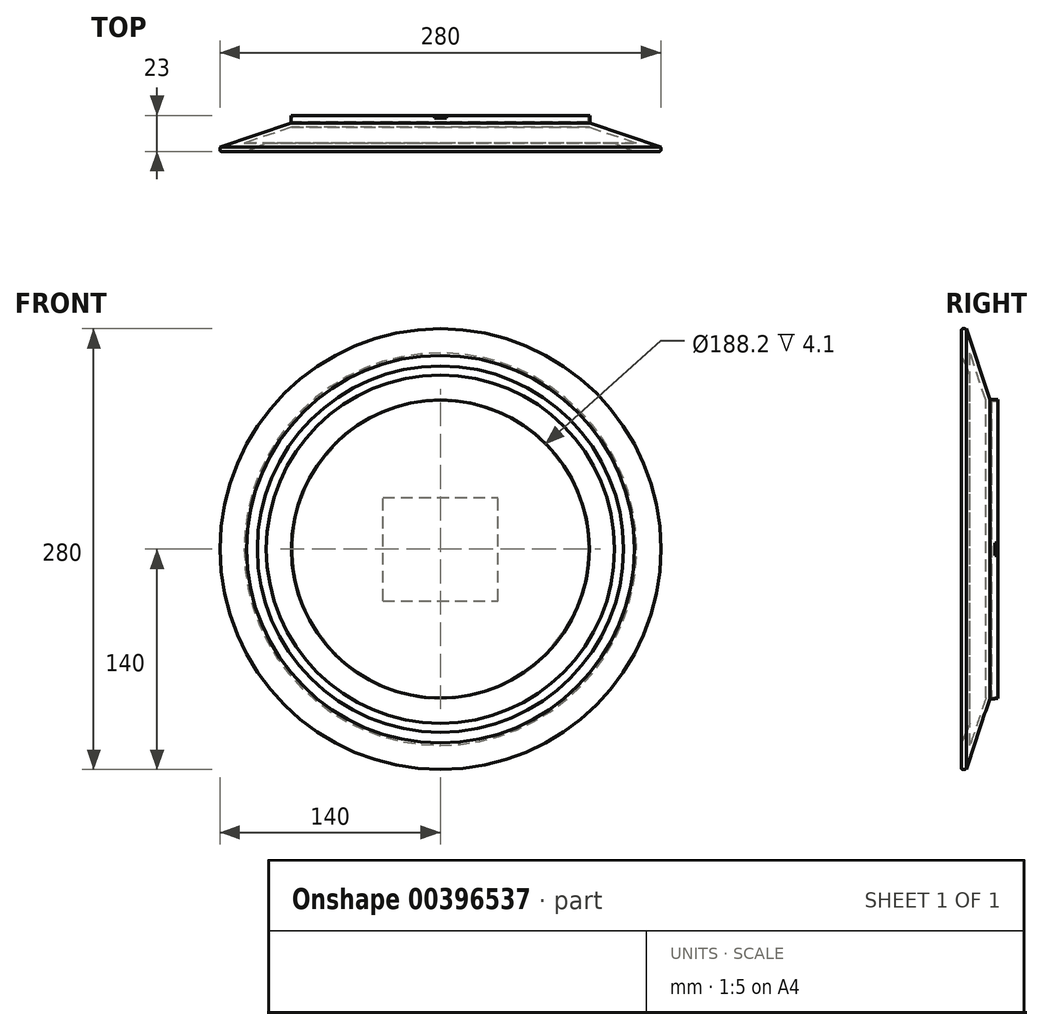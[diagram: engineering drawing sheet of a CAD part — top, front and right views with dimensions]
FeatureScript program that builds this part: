
annotation { "Feature Type Name" : "Feature", "Feature Type Description" : "" }
export const myFeature = defineFeature(function(context is Context, id is Id, definition is map)
    precondition{}
    {
        {
            var Q0;
            Q0=qCreatedBy(makeId("Front.planeOp"),FACE);
            var sketch = newSketch(context, id + "F0", { "sketchPlane" : qUnion([Q0])});
            skCircle(sketch, "E0", {"center": v(0, 0) * mm, "radius": 95 * mm});
            skSolve(sketch);
        }
        {
            var Q0;
            Q0=qSketchRegion(id+"F0",true);
            extrude(context, id + "F1", {"entities" : qUnion([Q0]), "depth" : 5 * mm});
        }
        {
            var Q0;
            Q0=makeQuery(id+"F1.opExtrude","CAP_FACE",FACE,{"disambiguationData":[OSD([sQuery(id+"F0.wireOp",EDGE,"E0")])],"isStart":true});
            shell(context, id + "F2", {"entities" : qUnion([Q0]), "thickness" : 0.9 * mm});
        }
        {
            var Q0;
            Q0=qCreatedBy(makeId("Front.planeOp"),FACE);
            cPlane(context, id + "F3", {"entities" : qUnion([Q0]), "cplaneType" : CPlaneType.OFFSET, "offset" : 20 * mm, "width" : 150 * mm, "height" : 150 * mm});
        }
        {
            var Q0;
            Q0=qCreatedBy(id+"F3.planeOp",FACE);
            var sketch = newSketch(context, id + "F4", { "sketchPlane" : qUnion([Q0])});
            skCircle(sketch, "E1", {"center": v(0, 0) * mm, "radius": 140 * mm});
            skSolve(sketch);
        }
        {
            var Q0;
            Q0=makeQuery(id+"F4.imprint","IMPRINT",FACE,{"disambiguationData":[TD([[makeQuery(id+"F4.imprint","IMPRINT",EDGE,{"derivedFrom":sQuery(id+"F4.wireOp",EDGE,"E1")}),1.0]])]});
            extrude(context, id + "F5", {"entities" : qUnion([Q0]), "depth" : 3 * mm});
        }
        {
            var Q0;
            Q0=makeQuery(id+"F1.opExtrude","CAP_FACE",FACE,{"disambiguationData":[OSD([sQuery(id+"F0.wireOp",EDGE,"E0")])],"isStart":false});
            var Q1;
            Q1=makeQuery(id+"F5.opExtrude","CAP_FACE",FACE,{"disambiguationData":[OSD([sQuery(id+"F4.wireOp",EDGE,"E1")])],"isStart":true});
            loft(context, id + "F6", {"sheetProfilesArray" : [{ "sheetProfileEntities" : qUnion([Q0]) }, { "sheetProfileEntities" : qUnion([Q1]) }]});
        }
        {
            var Q0;
            Q0=makeQuery(id+"F5.opExtrude","CAP_FACE",FACE,{"disambiguationData":[OSD([sQuery(id+"F4.wireOp",EDGE,"E1")])],"isStart":false});
            shell(context, id + "F7", {"entities" : qUnion([Q0]), "thickness" : 3 * mm});
        }
        {
            var Q0;
            Q0=makeQuery(id+"F5.opExtrude","CAP_EDGE",EDGE,{"disambiguationData":[OSD([sQuery(id+"F4.wireOp",EDGE,"E1")])],"isStart":true});
            var Q1;
            Q1=makeQuery(id+"F5.opExtrude","CAP_EDGE",EDGE,{"disambiguationData":[OSD([sQuery(id+"F4.wireOp",EDGE,"E1")])],"isStart":false});
            fillet(context, id + "F8", {"entities" : qUnion([Q0, Q1]), "radius" : 1 * mm, "tangentPropagation" : true, "allowEdgeOverflow" : false});
        }
        {
            var Q0;
            Q0=makeQuery(id+"F6.opLoft","SWEPT_FACE",FACE,{"disambiguationData":[OSD([sQuery(id+"F0.wireOp",EDGE,"E0"),sQuery(id+"F4.wireOp",EDGE,"E1")])]});
            var Q1;
            Q1=makeQuery(id+"F6.opLoft","SWEPT_BODY",BODY,{"disambiguationData":[OSD([sQuery(id+"F0.wireOp",EDGE,"E0"),sQuery(id+"F4.wireOp",EDGE,"E1")])]});
            shell(context, id + "F9", {"isHollow" : true, "entities" : qUnion([Q0]), "parts" : qUnion([Q1]), "thickness" : 2.5 * mm});
        }
        {
            var Q0;
            Q0=qCreatedBy(makeId("Top.planeOp"),FACE);
            var sketch = newSketch(context, id + "F10", { "sketchPlane" : qUnion([Q0])});
            skLineSegment(sketch, "E2.bottom", {"start": v(3.9, 1.63) * mm, "end": v(-3.9, 1.63) * mm});
            skLineSegment(sketch, "E2.top", {"start": v(3.9, -1.63) * mm, "end": v(-3.9, -1.63) * mm});
            skLineSegment(sketch, "E2.left", {"start": v(3.9, 1.63) * mm, "end": v(3.9, -1.63) * mm});
            skLineSegment(sketch, "E2.right", {"start": v(-3.9, 1.63) * mm, "end": v(-3.9, -1.63) * mm});
            skPoint(sketch, "E2.middle", {"position": v(0, 0) * mm});
            skSolve(sketch);
        }
        {
            var Q0;
            Q0=makeQuery(id+"F10.imprint","IMPRINT",FACE,{"disambiguationData":[TD([[makeQuery(id+"F10.imprint","IMPRINT",EDGE,{"derivedFrom":sQuery(id+"F10.wireOp",EDGE,"E2.bottom")}),1.0]])]});
            extrude(context, id + "F11", {"entities" : qUnion([Q0]), "operationType" : NewBodyOperationType.REMOVE, "oppositeDirection" : true, "depth" : 109.4 * mm, "hasSecondDirection" : true, "secondDirectionOppositeDirection" : false, "secondDirectionDepth" : 153.9 * mm});
        }
        {
            var Q0;
            Q0=qCreatedBy(makeId("Right.planeOp"),FACE);
            var sketch = newSketch(context, id + "F12", { "sketchPlane" : qUnion([Q0])});
            skLineSegment(sketch, "E3.bottom", {"start": v(1.8, -3.9) * mm, "end": v(-1.8, -3.9) * mm});
            skLineSegment(sketch, "E3.top", {"start": v(1.8, 3.9) * mm, "end": v(-1.8, 3.9) * mm});
            skLineSegment(sketch, "E3.left", {"start": v(1.8, -3.9) * mm, "end": v(1.8, 3.9) * mm});
            skLineSegment(sketch, "E3.right", {"start": v(-1.8, -3.9) * mm, "end": v(-1.8, 3.9) * mm});
            skPoint(sketch, "E3.middle", {"position": v(0, 0) * mm});
            skSolve(sketch);
        }
        {
            var Q0;
            Q0 = qSketchRegion(id + "F12", true);
            extrude(context, id + "F13", {"entities" : qUnion([Q0]), "operationType" : NewBodyOperationType.REMOVE, "oppositeDirection" : true, "depth" : 116 * mm, "hasSecondDirection" : true, "secondDirectionOppositeDirection" : false, "secondDirectionDepth" : 123 * mm});
        }
        {
            var Q0;
            Q0=qCreatedBy(makeId("Front.planeOp"),FACE);
            var sketch = newSketch(context, id + "F14", { "sketchPlane" : qUnion([Q0])});
            skLineSegment(sketch, "E4.bottom", {"start": v(-36.58, -32.8) * mm, "end": v(36.58, -32.8) * mm});
            skLineSegment(sketch, "E4.top", {"start": v(-36.58, 32.8) * mm, "end": v(36.58, 32.8) * mm});
            skLineSegment(sketch, "E4.left", {"start": v(-36.58, -32.8) * mm, "end": v(-36.58, 32.8) * mm});
            skLineSegment(sketch, "E4.right", {"start": v(36.58, -32.8) * mm, "end": v(36.58, 32.8) * mm});
            skPoint(sketch, "E4.middle", {"position": v(0, 0) * mm});
            skSolve(sketch);
        }
        {
            var Q0;
            Q0=makeQuery(id+"F14.imprint","IMPRINT",FACE,{"disambiguationData":[TD([[makeQuery(id+"F14.imprint","IMPRINT",EDGE,{"derivedFrom":sQuery(id+"F14.wireOp",EDGE,"E4.bottom")}),1.0]])]});
            extrude(context, id + "F15", {"entities" : qUnion([Q0]), "depth" : 0.01 * mm});
        }
        {
            var Q0;
            Q0=qCreatedBy(makeId("Top.planeOp"),FACE);
            var sketch = newSketch(context, id + "F16", { "sketchPlane" : qUnion([Q0])});
            skLineSegment(sketch, "E5", {"start": v(0, -9.8) * mm, "end": v(0, -30.26) * mm, "construction": true});
            skLineSegment(sketch, "E6", {"start": v(0, -9.8) * mm, "end": v(93.1, -9.8) * mm});
            skLineSegment(sketch, "E7", {"start": v(93.1, -9.8) * mm, "end": v(126.54, -24.5) * mm});
            skLineSegment(sketch, "E8", {"start": v(126.54, -24.5) * mm, "end": v(0, -30.26) * mm});
            skLineSegment(sketch, "E9", {"start": v(0, -9.8) * mm, "end": v(0, -30.26) * mm});
            skSolve(sketch);
        }
        {
            var Q0;
            Q0=makeQuery(id+"F16.imprint","IMPRINT",FACE,{"disambiguationData":[TD([[makeQuery(id+"F16.imprint","IMPRINT",EDGE,{"derivedFrom":sQuery(id+"F16.wireOp",EDGE,"E6")}),-1.0]])]});
            var Q1;
            Q1=sQuery(id+"F16.wireOp",EDGE,"E9");
            revolve(context, id + "F17", {"operationType" : NewBodyOperationType.REMOVE, "entities" : qUnion([Q0]), "axis" : qUnion([Q1]), "revolveType" : RevolveType.FULL, "oppositeDirection" : true});
        }
    });
